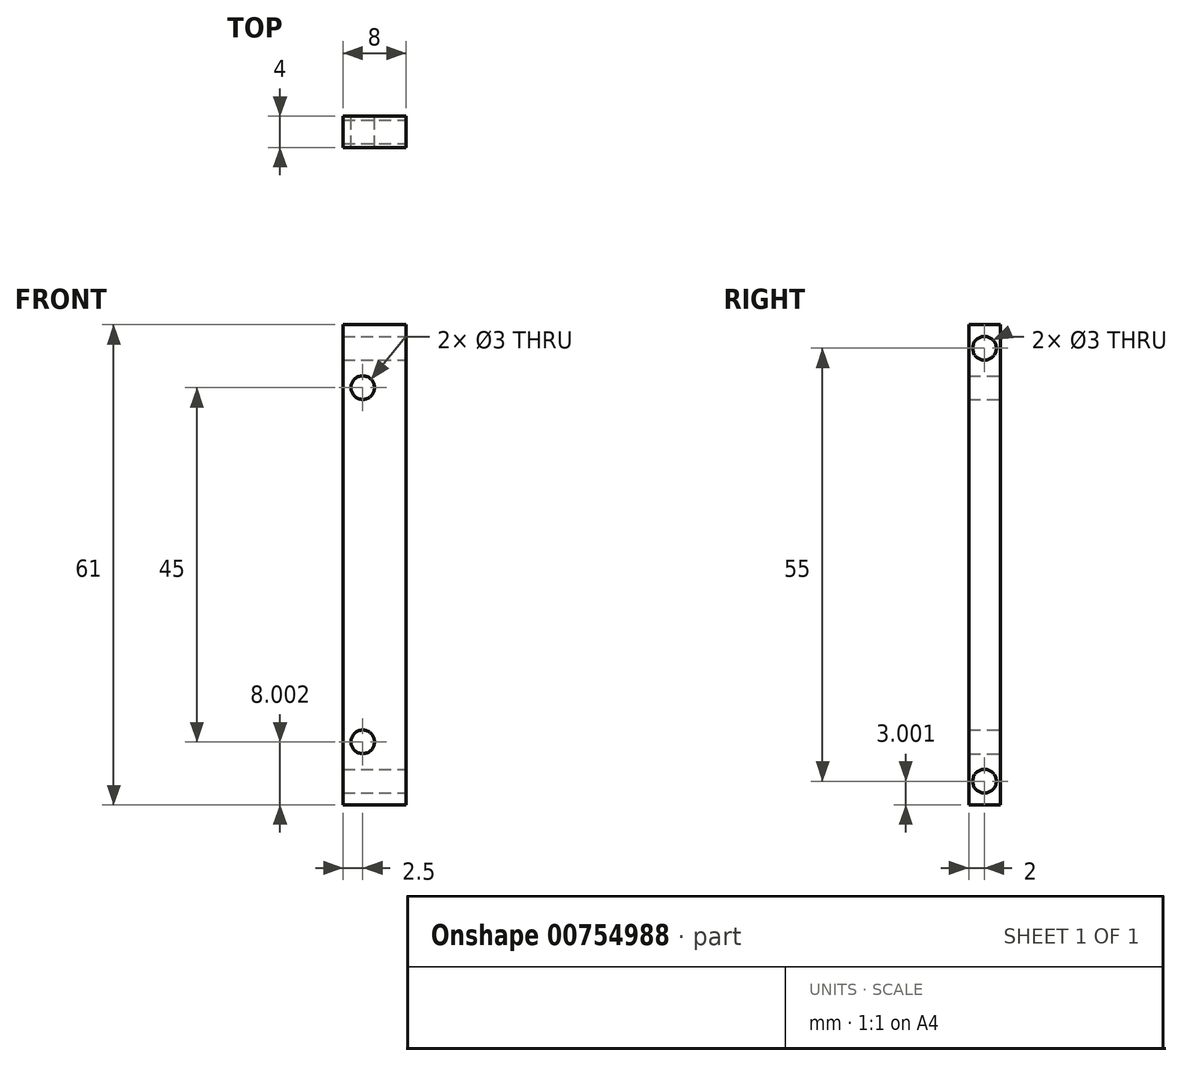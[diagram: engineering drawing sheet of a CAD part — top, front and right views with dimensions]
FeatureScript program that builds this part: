
annotation { "Feature Type Name" : "Feature", "Feature Type Description" : "" }
export const myFeature = defineFeature(function(context is Context, id is Id, definition is map)
    precondition{}
    {
        {
            var Q0;
            Q0=qCreatedBy(makeId("Front.planeOp"),FACE);
            var sketch = newSketch(context, id + "F0", { "sketchPlane" : qUnion([Q0])});
            skLineSegment(sketch, "E0.bottom", {"start": v(-8, 52.13) * mm, "end": v(0, 52.13) * mm});
            skLineSegment(sketch, "E0.top", {"start": v(-8, -12.87) * mm, "end": v(0, -12.87) * mm});
            skLineSegment(sketch, "E0.left", {"start": v(-8, 52.13) * mm, "end": v(-8, -12.87) * mm});
            skLineSegment(sketch, "E0.right", {"start": v(0, 52.13) * mm, "end": v(0, -12.87) * mm});
            skCircle(sketch, "E1", {"center": v(-5.5, 42.13) * mm, "radius": 1.5 * mm});
            skCircle(sketch, "E2", {"center": v(-5.5, -2.87) * mm, "radius": 1.5 * mm});
            skSolve(sketch);
        }
        {
            var Q0;
            Q0=makeQuery(id+"F0.imprint","IMPRINT",FACE,{"disambiguationData":[TD([[makeQuery(id+"F0.imprint","IMPRINT",EDGE,{"derivedFrom":sQuery(id+"F0.wireOp",EDGE,"E0.bottom")}),-1.0]])]});
            extrude(context, id + "F1", {"entities" : qUnion([Q0]), "depth" : 4 * mm, "offsetDistance" : 25 * mm});
        }
        {
            var Q0;
            Q0=makeQuery(id+"F1.opExtrude","SWEPT_FACE",FACE,{"disambiguationData":[OSD([sQuery(id+"F0.wireOp",EDGE,"E0.right")])]});
            var sketch = newSketch(context, id + "F2", { "sketchPlane" : qUnion([Q0])});
            skCircle(sketch, "E3", {"center": v(-2, 47.13) * mm, "radius": 1.5 * mm});
            skPoint(sketch, "E3.centerSnap0", {"position": v(-2, 52.13) * mm});
            skCircle(sketch, "E4", {"center": v(-2, -7.87) * mm, "radius": 1.5 * mm});
            skPoint(sketch, "E4.centerSnap0", {"position": v(-2, -12.87) * mm});
            skSolve(sketch);
        }
        {
            var Q0;
            Q0 = qSketchRegion(id + "F2", true);
            extrude(context, id + "F3", {"entities" : qUnion([Q0]), "operationType" : NewBodyOperationType.REMOVE, "oppositeDirection" : true, "depth" : 25 * mm, "offsetDistance" : 25 * mm});
        }
        {
            var Q0;
            Q0=makeQuery(id+"F1.opExtrude","SWEPT_FACE",FACE,{"disambiguationData":[OSD([sQuery(id+"F0.wireOp",EDGE,"E0.right")])]});
            var sketch = newSketch(context, id + "F4", { "sketchPlane" : qUnion([Q0])});
            skLineSegment(sketch, "E5.bottom", {"start": v(-7.25, 53.3) * mm, "end": v(2.34, 53.3) * mm});
            skLineSegment(sketch, "E5.top", {"start": v(-7.25, 50.13) * mm, "end": v(2.34, 50.13) * mm});
            skLineSegment(sketch, "E5.left", {"start": v(-7.25, 53.3) * mm, "end": v(-7.25, 50.13) * mm});
            skLineSegment(sketch, "E5.right", {"start": v(2.34, 53.3) * mm, "end": v(2.34, 50.13) * mm});
            skLineSegment(sketch, "E6.bottom", {"start": v(-5.01, -13.9) * mm, "end": v(4.2, -13.9) * mm});
            skLineSegment(sketch, "E6.top", {"start": v(-5.01, -10.87) * mm, "end": v(4.2, -10.87) * mm});
            skLineSegment(sketch, "E6.left", {"start": v(-5.01, -13.9) * mm, "end": v(-5.01, -10.87) * mm});
            skLineSegment(sketch, "E6.right", {"start": v(4.2, -13.9) * mm, "end": v(4.2, -10.87) * mm});
            skSolve(sketch);
        }
        {
            var Q0;
            Q0 = qSketchRegion(id + "F4", true);
            extrude(context, id + "F5", {"entities" : qUnion([Q0]), "operationType" : NewBodyOperationType.REMOVE, "oppositeDirection" : true, "depth" : 25 * mm, "offsetDistance" : 25 * mm});
        }
    });
